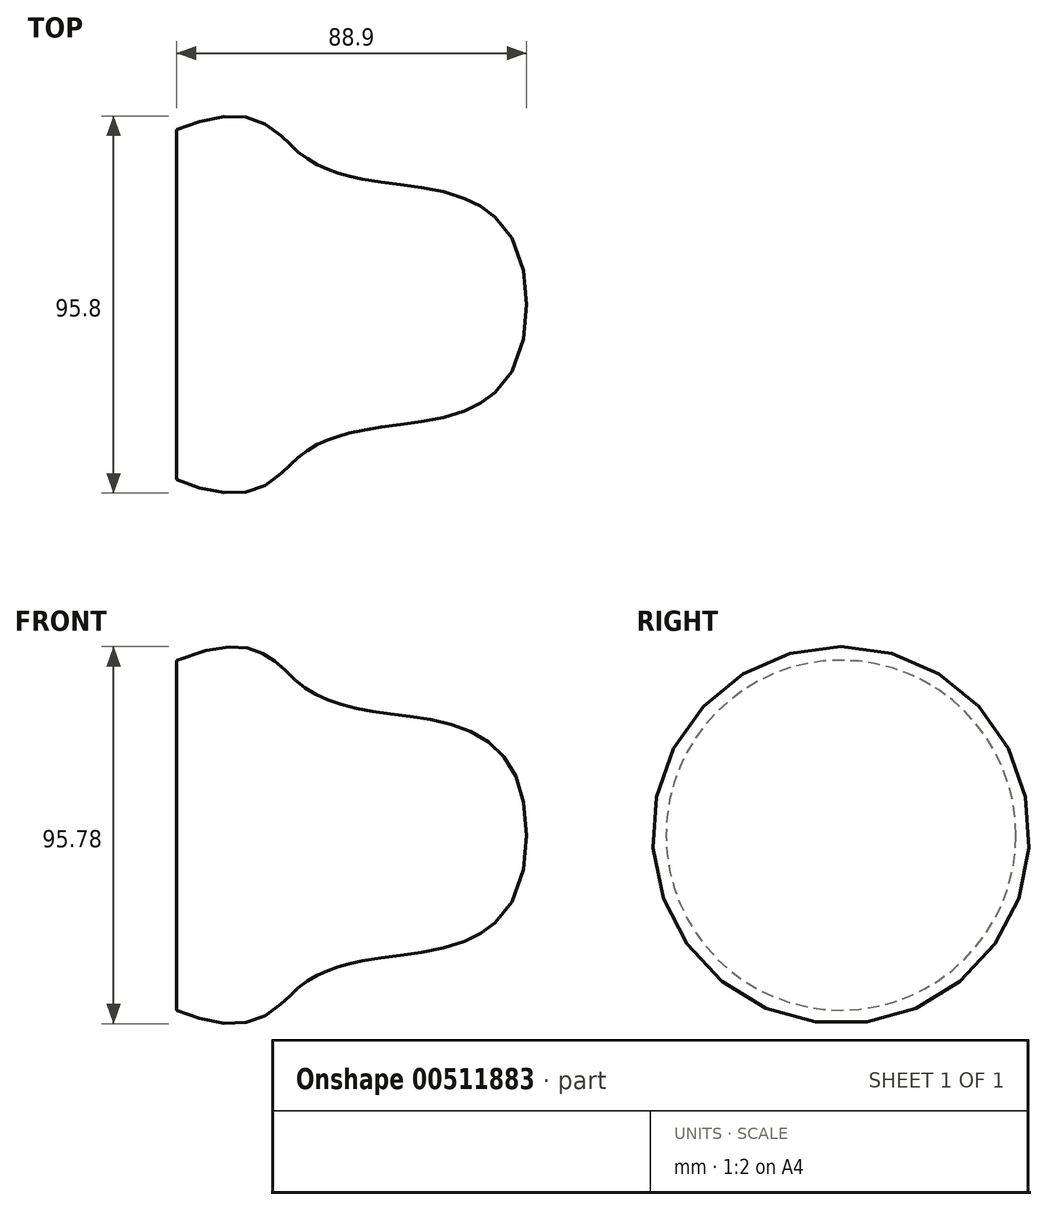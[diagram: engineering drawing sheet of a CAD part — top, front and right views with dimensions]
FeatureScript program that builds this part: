
annotation { "Feature Type Name" : "Feature", "Feature Type Description" : "" }
export const myFeature = defineFeature(function(context is Context, id is Id, definition is map)
    precondition{}
    {
        {
            var Q0;
            Q0=qCreatedBy(makeId("Front.planeOp"),FACE);
            var sketch = newSketch(context, id + "F0", { "sketchPlane" : qUnion([Q0])});
            skLineSegment(sketch, "E0", {"start": v(0, 0) * mm, "end": v(0, 44.45) * mm});
            skLineSegment(sketch, "E1", {"start": v(0, 0) * mm, "end": v(88.9, 0) * mm});
            skLineSegment(sketch, "E2", {"start": v(88.9, 0) * mm, "end": v(88.9, 27.86) * mm});
            skFitSpline(sketch, "E3", {"points": [v(88.9, 0) * mm, v(54.35, 30.8) * mm, v(31.15, 38.59) * mm, v(0, 44.45) * mm], "startDerivative": vector(0, 213.47) * mm, "endDerivative": vector(-189.97, -77.95) * mm});
            skSolve(sketch);
        }
        {
            var Q0;
            Q0 = qSketchRegion(id + "F0", true);
            var Q1;
            Q1=sQuery(id+"F0.wireOp",EDGE,"E1");
            revolve(context, id + "F1", {"entities" : qUnion([Q0]), "axis" : qUnion([Q1]), "revolveType" : RevolveType.FULL});
        }
    });
